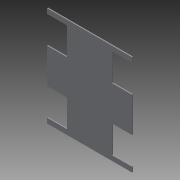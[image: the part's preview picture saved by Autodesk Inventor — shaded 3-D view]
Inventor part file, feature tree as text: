
AUTODESK INVENTOR PART (.ipt)
format: ipt  version: 2014 (Build 180170000, 170)  size: 98,304 bytes
history: native  units: mm
features: extrude x1, sketch x1
ambient origin geometry x8: Origin, YZ Plane, XZ Plane, XY Plane, X Axis, Y Axis, Z Axis, Center Point
bodies: Volumenkörper1 (feature_tree)
feature tree (2):
  extrude  "Extrusion1"  Depth=80.0mm
  sketch  "Skizze1"  dims[d17=180.0mm d19=80.0mm d23=140.0mm d25=20.0mm d26=4.0mm d27=0.0mm]
